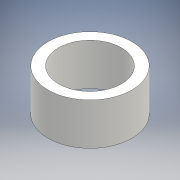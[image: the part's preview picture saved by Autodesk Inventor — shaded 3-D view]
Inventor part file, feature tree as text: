
AUTODESK INVENTOR PART (.ipt)
format: ipt  version: 2016 (Build 200138000, 138)  size: 90,624 bytes
history: native  units: mm
features: other x1, extrude x1, sketch x1
ambient origin geometry x8: Origin, YZ Plane, XZ Plane, XY Plane, X Axis, Y Axis, Z Axis, Center Point
bodies: Body1 (feature_tree)
feature tree (3):
  other  "ソリッド1"
  extrude  "押し出し1"  Depth=6.0mm
  sketch  "スケッチ1"
